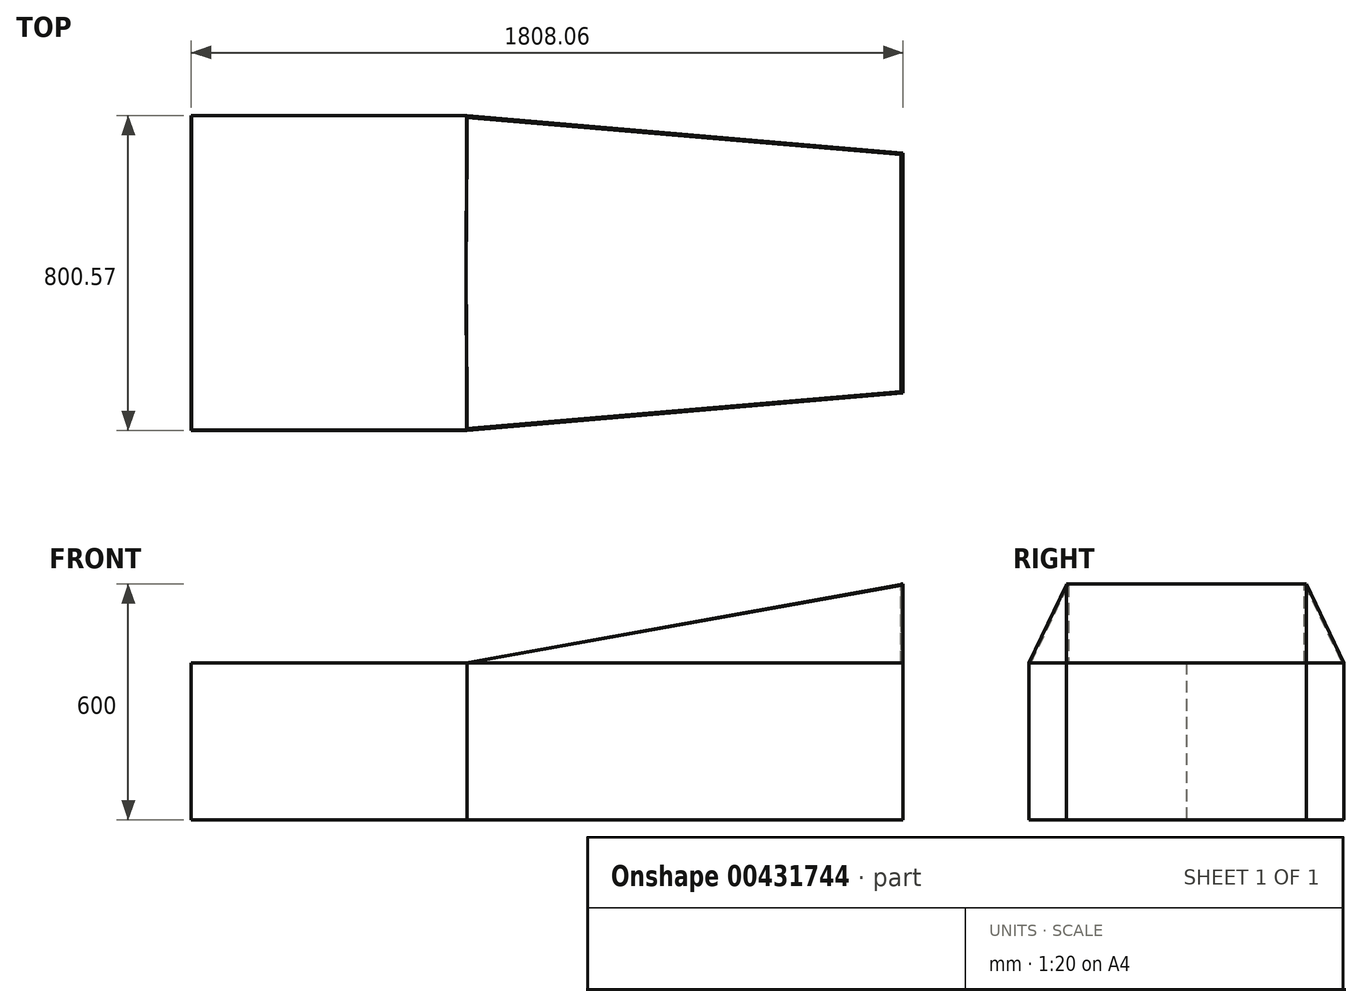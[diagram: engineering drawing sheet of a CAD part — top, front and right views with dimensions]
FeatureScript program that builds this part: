
annotation { "Feature Type Name" : "Feature", "Feature Type Description" : "" }
export const myFeature = defineFeature(function(context is Context, id is Id, definition is map)
    precondition{}
    {
        {
            var Q0;
            Q0=qCreatedBy(makeId("Top.planeOp"),FACE);
            var sketch = newSketch(context, id + "F0", { "sketchPlane" : qUnion([Q0])});
            skLineSegment(sketch, "E0", {"start": v(-87.38, -400) * mm, "end": v(1020.48, -305) * mm});
            skLineSegment(sketch, "E1", {"start": v(1020.48, -305) * mm, "end": v(1020.48, 0) * mm});
            skLineSegment(sketch, "E2", {"start": v(1020.48, 0) * mm, "end": v(-89.52, 0) * mm});
            skLineSegment(sketch, "E3", {"start": v(-89.52, 0) * mm, "end": v(-87.38, -400) * mm});
            skLineSegment(sketch, "E4.MirrorCS", {"start": v(-89.52, 0) * mm, "end": v(-87.38, 400) * mm});
            skLineSegment(sketch, "E5.MirrorCS", {"start": v(1020.48, 305) * mm, "end": v(1020.48, 0) * mm});
            skLineSegment(sketch, "E6.MirrorCS", {"start": v(-87.38, 400) * mm, "end": v(1020.48, 305) * mm});
            skSolve(sketch);
        }
        {
            var Q0;
            Q0=qCreatedBy(makeId("Top.planeOp"),FACE);
            var sketch = newSketch(context, id + "F1", { "sketchPlane" : qUnion([Q0])});
            skLineSegment(sketch, "E7.bottom", {"start": v(-87.32, -399.42) * mm, "end": v(-787.32, -399.42) * mm});
            skLineSegment(sketch, "E7.top", {"start": v(-87.32, 400.58) * mm, "end": v(-787.32, 400.58) * mm});
            skLineSegment(sketch, "E7.left", {"start": v(-87.32, -399.42) * mm, "end": v(-87.32, 400.58) * mm});
            skLineSegment(sketch, "E7.right", {"start": v(-787.32, -399.42) * mm, "end": v(-787.32, 400.58) * mm});
            skSolve(sketch);
        }
        {
            var Q0;
            Q0=makeQuery(id+"F1.imprint","IMPRINT",FACE,{"disambiguationData":[TD([[makeQuery(id+"F1.imprint","IMPRINT",EDGE,{"derivedFrom":sQuery(id+"F1.wireOp",EDGE,"E7.bottom")}),-1.0]])]});
            extrude(context, id + "F2", {"entities" : qUnion([Q0]), "depth" : 400 * mm});
        }
        {
            var Q0;
            Q0=makeQuery(id+"F2.opExtrude","CAP_FACE",FACE,{"disambiguationData":[OSD([sQuery(id+"F1.wireOp",EDGE,"E7.bottom"),sQuery(id+"F1.wireOp",EDGE,"E7.top"),sQuery(id+"F1.wireOp",EDGE,"E7.left"),sQuery(id+"F1.wireOp",EDGE,"E7.right")])],"isStart":false});
            shell(context, id + "F3", {"entities" : qUnion([Q0]), "thickness" : 0.5 * mm});
        }
        {
            var Q0;
            Q0=makeQuery(id+"F0.imprint","IMPRINT",FACE,{"disambiguationData":[TD([[makeQuery(id+"F0.imprint","IMPRINT",EDGE,{"derivedFrom":sQuery(id+"F0.wireOp",EDGE,"E2")}),-1.0]])]});
            var Q1;
            Q1=makeQuery(id+"F0.imprint","IMPRINT",FACE,{"disambiguationData":[TD([[makeQuery(id+"F0.imprint","IMPRINT",EDGE,{"derivedFrom":sQuery(id+"F0.wireOp",EDGE,"E0")}),1.0]])]});
            extrude(context, id + "F4", {"entities" : qUnion([Q0, Q1]), "operationType" : NewBodyOperationType.ADD, "depth" : 400 * mm});
        }
        {
            var Q0;
            Q0=makeQuery(id+"F4.boolean.opBoolean","MERGE",FACE,{"derivedFrom":[makeQuery(id+"F2.opExtrude","CAP_FACE",FACE,{"disambiguationData":[OSD([sQuery(id+"F1.wireOp",EDGE,"E7.bottom"),sQuery(id+"F1.wireOp",EDGE,"E7.top"),sQuery(id+"F1.wireOp",EDGE,"E7.left"),sQuery(id+"F1.wireOp",EDGE,"E7.right")])],"isStart":false}),makeQuery(id+"F4.opExtrude","CAP_FACE",FACE,{"disambiguationData":[OSD([sQuery(id+"F0.wireOp",EDGE,"E0"),sQuery(id+"F0.wireOp",EDGE,"E1"),sQuery(id+"F0.wireOp",EDGE,"E3"),sQuery(id+"F0.wireOp",EDGE,"E4.MirrorCS"),sQuery(id+"F0.wireOp",EDGE,"E5.MirrorCS"),sQuery(id+"F0.wireOp",EDGE,"E6.MirrorCS")])],"isStart":false})]});
            shell(context, id + "F5", {"entities" : qUnion([Q0]), "thickness" : 0.5 * mm});
        }
        {
            var Q0;
            Q0=makeQuery(id+"F4.opExtrude","SWEPT_FACE",FACE,{"disambiguationData":[OSD([sQuery(id+"F0.wireOp",EDGE,"E1"),sQuery(id+"F0.wireOp",EDGE,"E5.MirrorCS")])]});
            var sketch = newSketch(context, id + "F6", { "sketchPlane" : qUnion([Q0])});
            skLineSegment(sketch, "E8", {"start": v(-305, 400) * mm, "end": v(-305, 600) * mm});
            skLineSegment(sketch, "E9", {"start": v(-305, 600) * mm, "end": v(305, 600) * mm});
            skLineSegment(sketch, "E10", {"start": v(305, 600) * mm, "end": v(305, 400) * mm});
            skSolve(sketch);
        }
        {
            var Q0;
            Q0=makeQuery(id+"F4.opExtrude","SWEPT_FACE",FACE,{"disambiguationData":[OSD([sQuery(id+"F0.wireOp",EDGE,"E0")])]});
            var sketch = newSketch(context, id + "F7", { "sketchPlane" : qUnion([Q0])});
            skLineSegment(sketch, "E11", {"start": v(-121.24, 400) * mm, "end": v(990.95, 597.56) * mm});
            skLineSegment(sketch, "E12", {"start": v(990.95, 597.56) * mm, "end": v(990.7, 400) * mm});
            skLineSegment(sketch, "E13", {"start": v(990.7, 400) * mm, "end": v(-121.24, 400) * mm});
            skSolve(sketch);
        }
        {
            var Q0;
            Q0=makeQuery(id+"F7.imprint","IMPRINT",FACE,{"disambiguationData":[TD([[makeQuery(id+"F7.imprint","IMPRINT",EDGE,{"derivedFrom":sQuery(id+"F7.wireOp",EDGE,"E11")}),-1.0]])]});
            extrude(context, id + "F8", {"entities" : qUnion([Q0]), "oppositeDirection" : true, "depth" : 5 * mm});
        }
        {
            var Q0;
            Q0=makeQuery(id+"F6.imprint","IMPRINT",FACE,{"disambiguationData":[TD([[makeQuery(id+"F6.imprint","IMPRINT",EDGE,{"derivedFrom":sQuery(id+"F6.wireOp",EDGE,"E8")}),-1.0]])]});
            extrude(context, id + "F9", {"entities" : qUnion([Q0]), "oppositeDirection" : true, "depth" : 5 * mm});
        }
        {
            var Q0;
            Q0=makeQuery(id+"F4.opExtrude","SWEPT_FACE",FACE,{"disambiguationData":[OSD([sQuery(id+"F0.wireOp",EDGE,"E6.MirrorCS")])]});
            var sketch = newSketch(context, id + "F10", { "sketchPlane" : qUnion([Q0])});
            skLineSegment(sketch, "E14", {"start": v(-990.7, 599.47) * mm, "end": v(121.18, 400) * mm});
            skLineSegment(sketch, "E15", {"start": v(121.18, 400) * mm, "end": v(-990.7, 400) * mm});
            skLineSegment(sketch, "E16", {"start": v(-990.7, 400) * mm, "end": v(-990.7, 599.47) * mm});
            skSolve(sketch);
        }
        {
            var Q0;
            Q0=makeQuery(id+"F10.imprint","IMPRINT",FACE,{"disambiguationData":[TD([[makeQuery(id+"F10.imprint","IMPRINT",EDGE,{"derivedFrom":sQuery(id+"F10.wireOp",EDGE,"E14")}),-1.0]])]});
            extrude(context, id + "F11", {"entities" : qUnion([Q0]), "oppositeDirection" : true, "depth" : 5 * mm});
        }
    });
